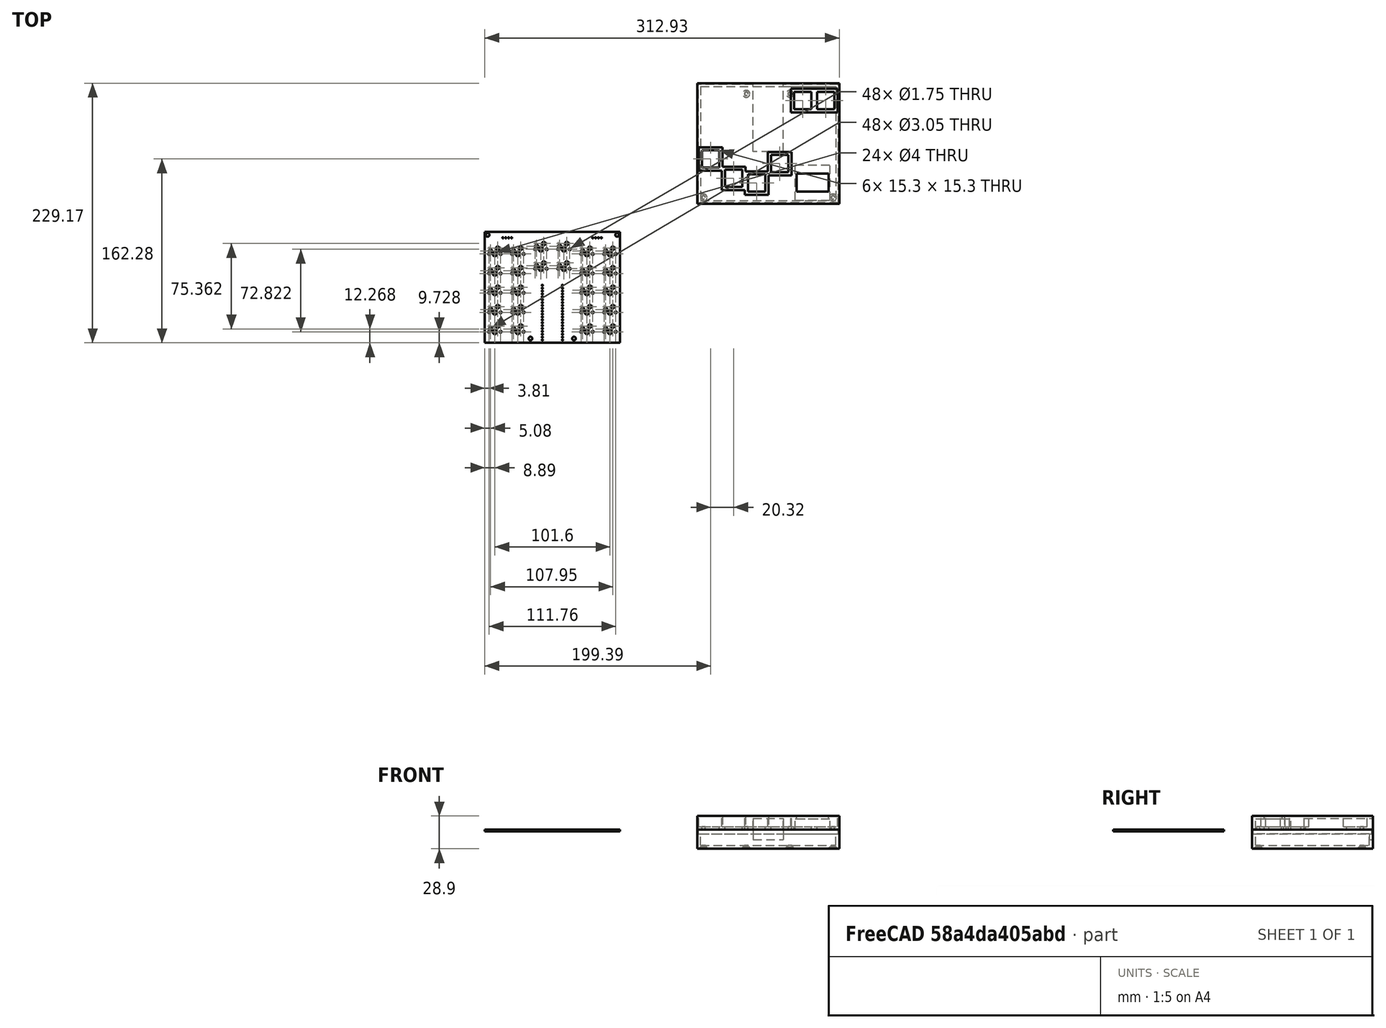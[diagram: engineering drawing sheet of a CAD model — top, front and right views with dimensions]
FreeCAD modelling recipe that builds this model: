
FCSTD DOCUMENT  (FreeCAD 0.20R29603 (Git))
Label: PCB and case
License: All rights reserved
LicenseURL: http://en.wikipedia.org/wiki/All_rights_reserved
objects: Part::Feature×3, App::Part×3, PartDesign::CoordinateSystem×1, Sketcher::SketchObject×1
note: 5 computed .brp shape members not serialized (recipe doc carries the construction recipe); baked Part::Feature solids carry a one-line shape summary decoded from their .brp

FEATURE [Part::Feature] Shape
  shape: bbox 125.5 x 106.5 x 11.9 mm, 82 faces (baked)
FEATURE [Part::Feature] Shape001
  Placement = pos=(0,0,33) rot=(0,0,1;0rad)
  shape: bbox 125.5 x 106.5 x 17 mm, 32 faces (baked)
FEATURE [PartDesign::CoordinateSystem] Local_CS_e212
  AttacherType = Attacher::AttachEngine3D
  MapMode = 2
  Support = -> [X_Axis001]
FEATURE [Sketcher::SketchObject] PCB_Sketch_e212
  FullyConstrained = false
  sketch-geometry (8):
    g0: LineSegment StartX=-86.36 StartY=7.62 StartZ=0 EndX=33.02 EndY=7.62 EndZ=0
    g1: LineSegment StartX=33.02 StartY=7.62 StartZ=0 EndX=33.02 EndY=-90.17 EndZ=0
    g2: LineSegment StartX=33.02 StartY=-90.17 StartZ=0 EndX=-86.36 EndY=-90.17 EndZ=0
    g3: LineSegment StartX=-86.36 StartY=-90.17 StartZ=0 EndX=-86.36 EndY=7.62 EndZ=0
    g4: Circle CenterX=30.48 CenterY=5.08 CenterZ=0 NormalX=0 NormalY=0 NormalZ=1 AngleXU=0 Radius=1.6
    g5: Circle CenterX=-7.62 CenterY=-86.36 CenterZ=0 NormalX=0 NormalY=0 NormalZ=1 AngleXU=0 Radius=1.6
    g6: Circle CenterX=-83.82 CenterY=5.08 CenterZ=0 NormalX=0 NormalY=0 NormalZ=1 AngleXU=0 Radius=1.6
    g7: Circle CenterX=-46.05 CenterY=-86.36 CenterZ=0 NormalX=0 NormalY=0 NormalZ=1 AngleXU=0 Radius=1.6
  constraints (4):
    c: Coincident(g2,g3)
    c: Coincident(g0,g3)
    c: Coincident(g1,g2)
    c: Coincident(g0,g1)
FEATURE [Part::Feature] Pcb_e212
  Placement = pos=(-190.5,43.18,0) rot=(0,0,1;0rad)
  shape: bbox 119.4 x 97.79 x 1.6 mm, 178 faces (baked)
FEATURE [App::Part] Board_Geoms_e212
  Group = -> [Pcb_e212,PCB_Sketch_e212]
  Origin = -> Origin
FEATURE [App::Part] Step_Models_e212
  Origin = -> Origin002
FEATURE [App::Part] Board_e212  label="PICO-blue-chords-pcb"
  Group = -> [Local_CS_e212,Board_Geoms_e212,Step_Models_e212]
  Origin = -> Origin001
  Placement = pos=(190.5,43.2,-4) rot=(1,0,0;3.14159rad)
